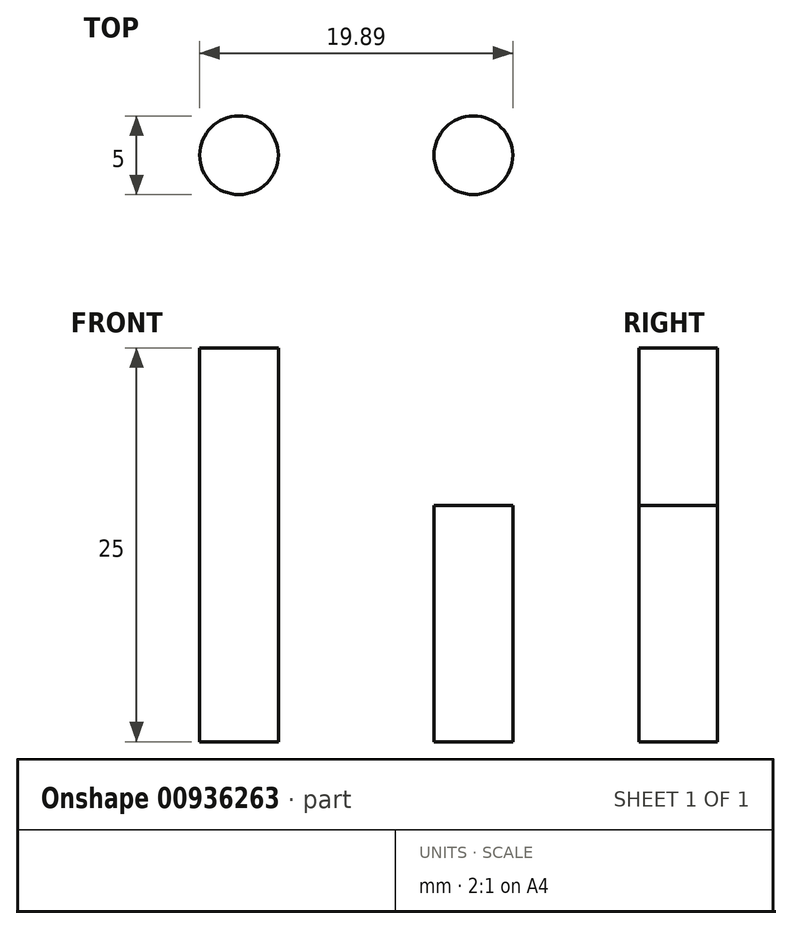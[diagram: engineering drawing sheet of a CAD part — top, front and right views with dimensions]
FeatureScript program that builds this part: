
annotation { "Feature Type Name" : "Feature", "Feature Type Description" : "" }
export const myFeature = defineFeature(function(context is Context, id is Id, definition is map)
    precondition{}
    {
        {
            var Q0;
            Q0=qCreatedBy(makeId("Top.planeOp"),FACE);
            var sketch = newSketch(context, id + "F0", { "sketchPlane" : qUnion([Q0])});
            skCircle(sketch, "E0", {"center": v(0, 0) * mm, "radius": 2.5 * mm});
            skSolve(sketch);
        }
        {
            var Q0;
            Q0=qSketchRegion(id+"F0",true);
            extrude(context, id + "F1", {"entities" : qUnion([Q0]), "depth" : 25 * mm, "offsetDistance" : 25 * mm});
        }
        {
            var Q0;
            Q0=qCreatedBy(makeId("Top.planeOp"),FACE);
            var sketch = newSketch(context, id + "F2", { "sketchPlane" : qUnion([Q0])});
            skCircle(sketch, "E1", {"center": v(14.89, 0) * mm, "radius": 2.5 * mm});
            skSolve(sketch);
        }
        {
            var Q0;
            Q0=qSketchRegion(id+"F2",true);
            extrude(context, id + "F3", {"entities" : qUnion([Q0]), "depth" : 15 * mm, "offsetDistance" : 25 * mm});
        }
    });
